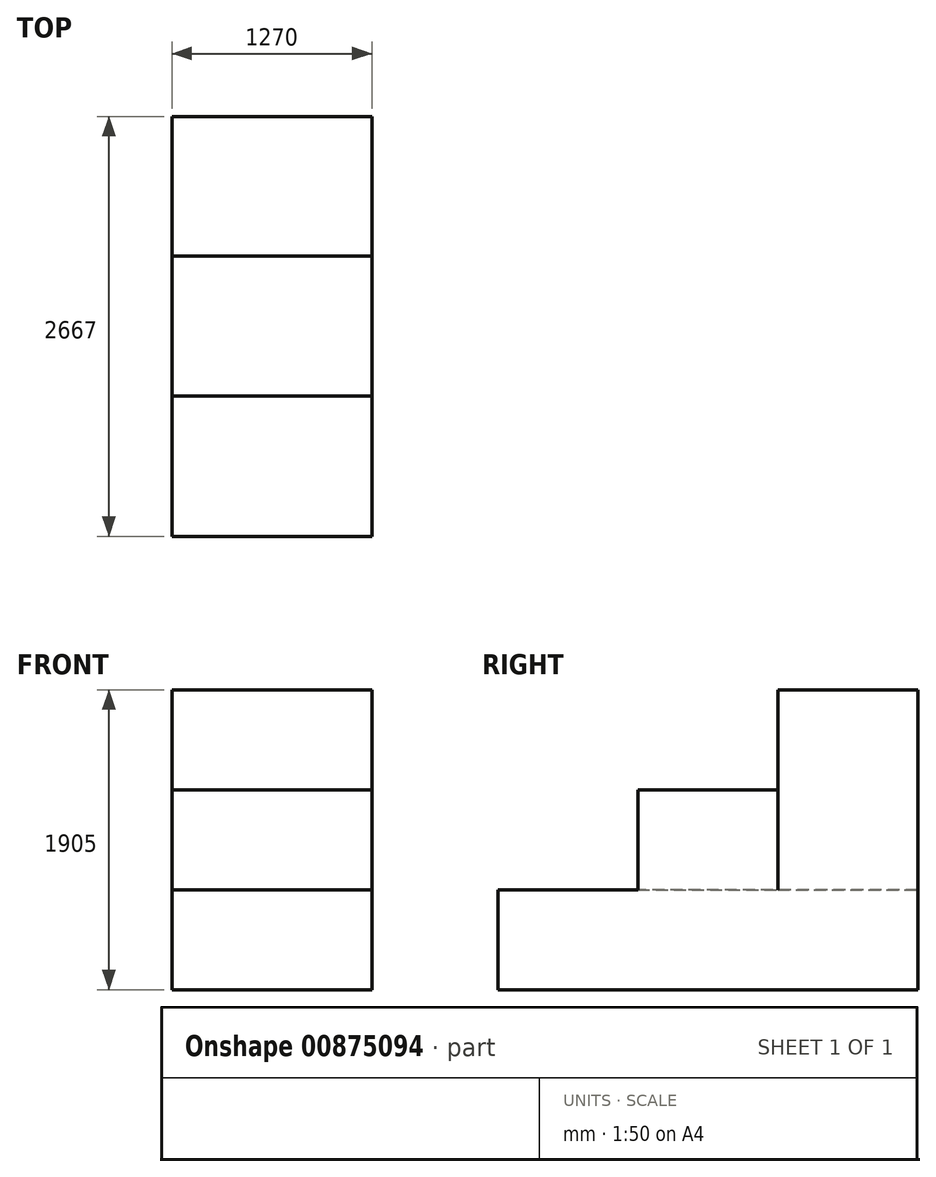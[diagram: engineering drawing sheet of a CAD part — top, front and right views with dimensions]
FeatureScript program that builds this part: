
annotation { "Feature Type Name" : "Feature", "Feature Type Description" : "" }
export const myFeature = defineFeature(function(context is Context, id is Id, definition is map)
    precondition{}
    {
        {
            var Q0;
            Q0=qCreatedBy(makeId("Front.planeOp"),FACE);
            var sketch = newSketch(context, id + "F0", { "sketchPlane" : qUnion([Q0])});
            skLineSegment(sketch, "E0.bottom", {"start": v(-153.17, -85.93) * mm, "end": v(1116.83, -85.93) * mm});
            skLineSegment(sketch, "E0.top", {"start": v(-153.17, 549.07) * mm, "end": v(1116.83, 549.07) * mm});
            skLineSegment(sketch, "E0.left", {"start": v(-153.17, -85.93) * mm, "end": v(-153.17, 549.07) * mm});
            skLineSegment(sketch, "E0.right", {"start": v(1116.83, -85.93) * mm, "end": v(1116.83, 549.07) * mm});
            skSolve(sketch);
        }
        {
            var Q0;
            Q0=makeQuery(id+"F0.imprint","IMPRINT",FACE,{"disambiguationData":[TD([[makeQuery(id+"F0.imprint","IMPRINT",EDGE,{"derivedFrom":sQuery(id+"F0.wireOp",EDGE,"E0.bottom")}),1.0]])]});
            extrude(context, id + "F1", {"entities" : qUnion([Q0]), "oppositeDirection" : true, "depth" : 2667 * mm, "offsetDistance" : 25.4 * mm});
        }
        {
            var Q0;
            Q0=makeQuery(id+"F1.opExtrude","SWEPT_FACE",FACE,{"disambiguationData":[OSD([sQuery(id+"F0.wireOp",EDGE,"E0.top")])]});
            var sketch = newSketch(context, id + "F2", { "sketchPlane" : qUnion([Q0])});
            skSolve(sketch);
        }
        {
            var Q0;
            {var subQ0=sQuery(id+"F0.wireOp",EDGE,"E0.top");Q0=makeQuery(id+"F2.imprint","IMPRINT",FACE,{"disambiguationData":[TD([[makeQuery(id+"F2.imprint","IMPRINT",EDGE,{"derivedFrom":makeQuery(id+"F1.opExtrude","CAP_EDGE",EDGE,{"disambiguationData":[OSD([subQ0])],"isStart":true})}),1.0]])]});}
            var sketch = newSketch(context, id + "F3", { "sketchPlane" : qUnion([Q0])});
            skLineSegment(sketch, "E1.bottom", {"start": v(-153.1, 889.27) * mm, "end": v(1116.9, 889.27) * mm});
            skLineSegment(sketch, "E1.top", {"start": v(-153.1, 1778.27) * mm, "end": v(1116.9, 1778.27) * mm});
            skLineSegment(sketch, "E1.left", {"start": v(-153.1, 889.27) * mm, "end": v(-153.1, 1778.27) * mm});
            skLineSegment(sketch, "E1.right", {"start": v(1116.9, 889.27) * mm, "end": v(1116.9, 1778.27) * mm});
            skSolve(sketch);
        }
        {
            var Q0;
            {var subQ0=sQuery(id+"F3.wireOp",EDGE,"E1.left");Q0=makeQuery(id+"F3.imprint","IMPRINT",FACE,{"disambiguationData":[TD([[makeQuery(id+"F3.imprint","IMPRINT",EDGE,{"derivedFrom":subQ0}),-1.0]])]});}
            extrude(context, id + "F4", {"entities" : qUnion([Q0]), "operationType" : NewBodyOperationType.ADD, "depth" : 635 * mm, "offsetDistance" : 25.4 * mm});
        }
        {
            var Q0;
            {var subQ0=sQuery(id+"F0.wireOp",EDGE,"E0.top");Q0=makeQuery(id+"F2.imprint","IMPRINT",FACE,{"disambiguationData":[TD([[makeQuery(id+"F2.imprint","IMPRINT",EDGE,{"derivedFrom":makeQuery(id+"F1.opExtrude","CAP_EDGE",EDGE,{"disambiguationData":[OSD([subQ0])],"isStart":true})}),1.0]])]});}
            var sketch = newSketch(context, id + "F5", { "sketchPlane" : qUnion([Q0])});
            skLineSegment(sketch, "E2.bottom", {"start": v(-152.95, 1778.55) * mm, "end": v(1117.05, 1778.55) * mm});
            skLineSegment(sketch, "E2.top", {"start": v(-152.95, 2667.55) * mm, "end": v(1117.05, 2667.55) * mm});
            skLineSegment(sketch, "E2.left", {"start": v(-152.95, 1778.55) * mm, "end": v(-152.95, 2667.55) * mm});
            skLineSegment(sketch, "E2.right", {"start": v(1117.05, 1778.55) * mm, "end": v(1117.05, 2667.55) * mm});
            skSolve(sketch);
        }
        {
            var Q0;
            {var subQ0=sQuery(id+"F5.wireOp",EDGE,"E2.left");var subQ1=sQuery(id+"F5.wireOp",EDGE,"E2.bottom");var subQ2=makeQuery(id+"F5.imprint","INTERSECT",VERTEX,{"derivedFrom":[subQ1,subQ0]});Q0=makeQuery(id+"F5.imprint","IMPRINT",FACE,{"disambiguationData":[TD([[makeQuery(id+"F5.imprint","IMPRINT",EDGE,{"disambiguationData":[TD([[subQ2,-1.0]])],"derivedFrom":subQ0}),-1.0]])]});}
            extrude(context, id + "F6", {"entities" : qUnion([Q0]), "operationType" : NewBodyOperationType.ADD, "depth" : 1270 * mm, "offsetDistance" : 25.4 * mm});
        }
    });
